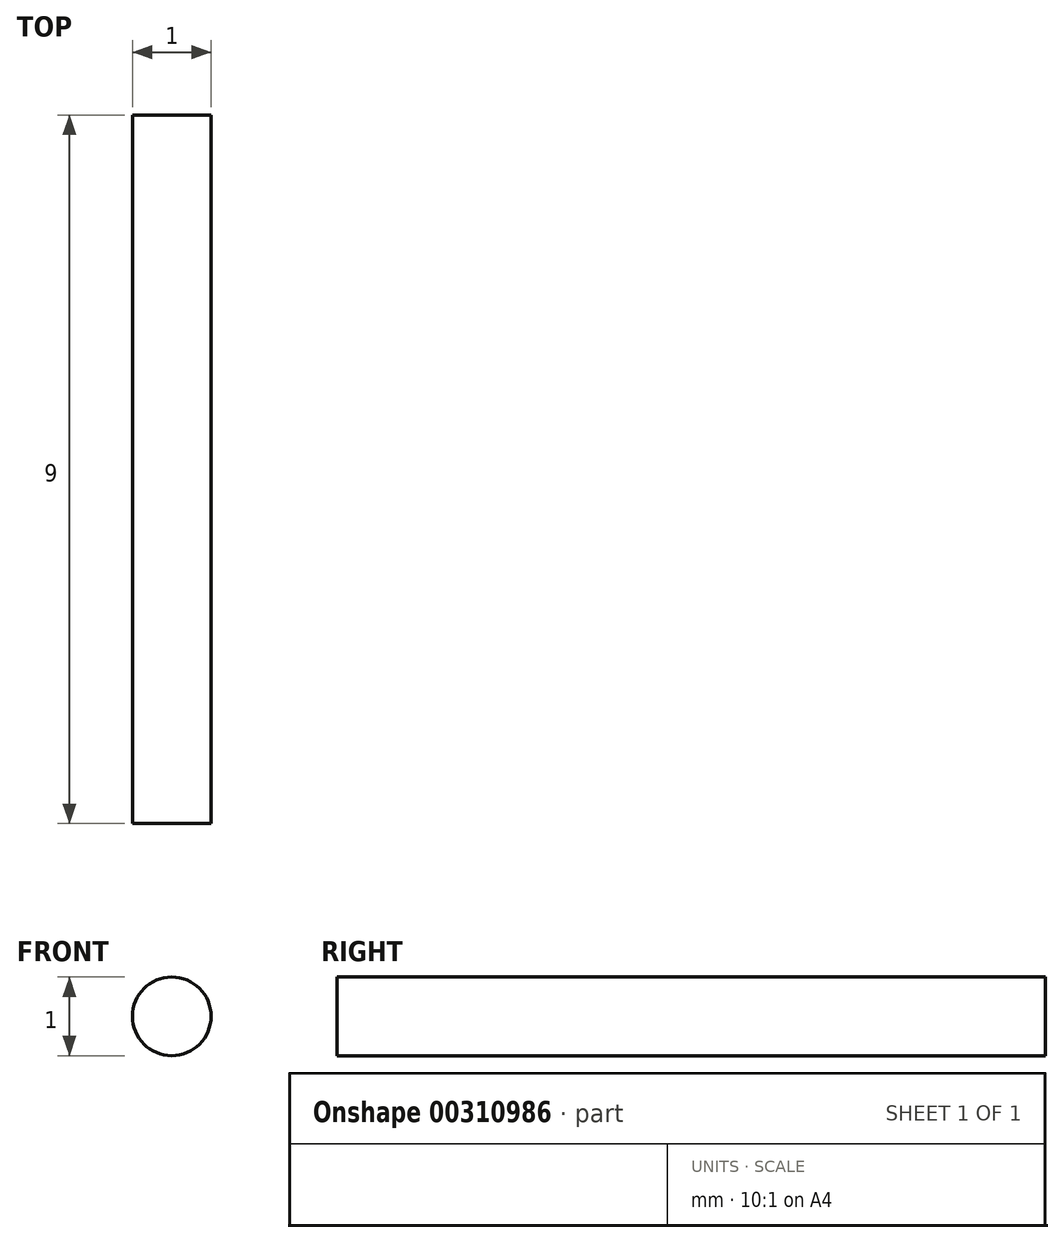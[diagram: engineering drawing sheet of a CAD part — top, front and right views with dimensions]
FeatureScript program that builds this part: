
annotation { "Feature Type Name" : "Feature", "Feature Type Description" : "" }
export const myFeature = defineFeature(function(context is Context, id is Id, definition is map)
    precondition{}
    {
        {
            var Q0;
            Q0=qCreatedBy(makeId("Front.planeOp"),FACE);
            var sketch = newSketch(context, id + "F0", { "sketchPlane" : qUnion([Q0])});
            skCircle(sketch, "E0", {"center": v(0, 0) * mm, "radius": 0.5 * mm});
            skSolve(sketch);
        }
        {
            var Q0;
            Q0=makeQuery(id+"F0.imprint","IMPRINT",FACE,{"disambiguationData":[TD([[makeQuery(id+"F0.imprint","IMPRINT",EDGE,{"derivedFrom":sQuery(id+"F0.wireOp",EDGE,"E0")}),1.0]])]});
            extrude(context, id + "F1", {"entities" : qUnion([Q0]), "depth" : 9 * mm});
        }
    });
